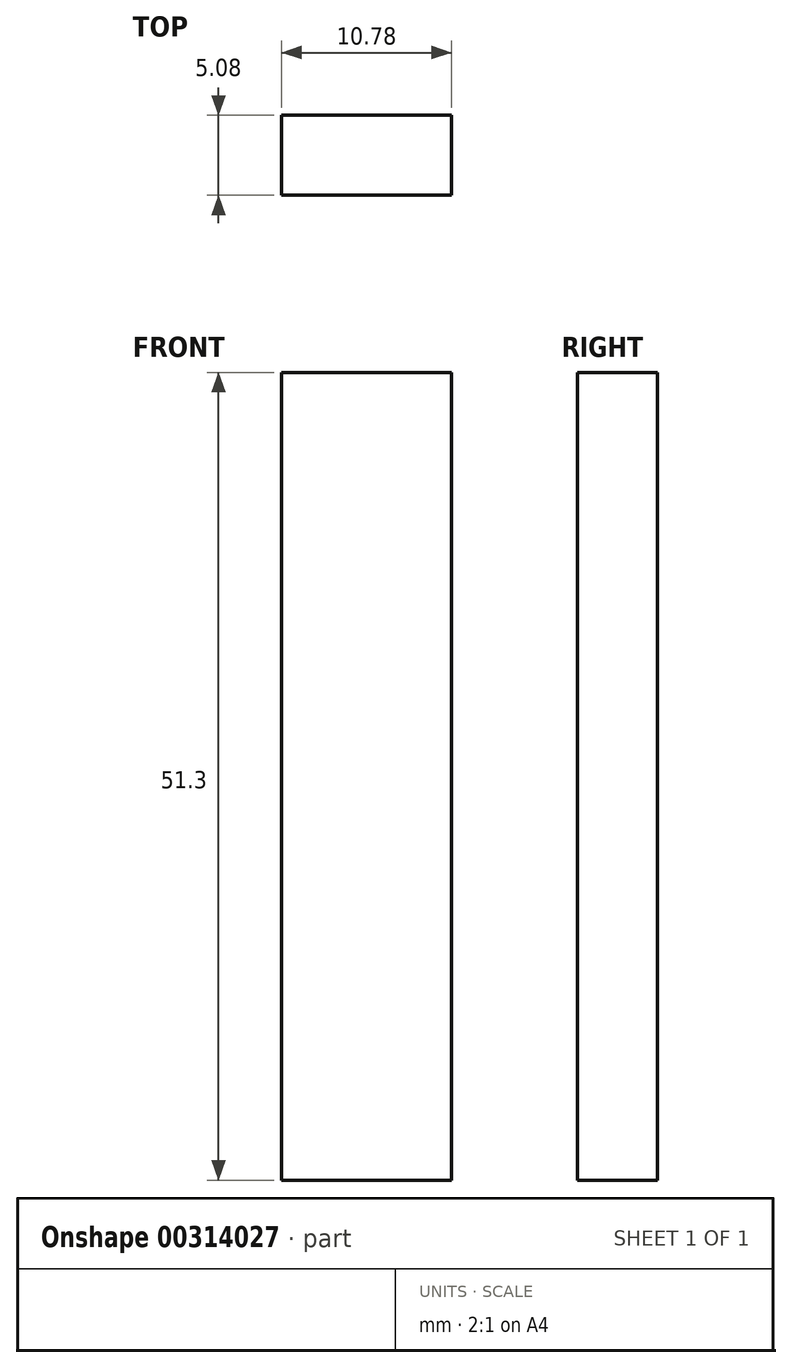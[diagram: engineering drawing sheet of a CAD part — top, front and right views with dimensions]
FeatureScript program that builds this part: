
annotation { "Feature Type Name" : "Feature", "Feature Type Description" : "" }
export const myFeature = defineFeature(function(context is Context, id is Id, definition is map)
    precondition{}
    {
        {
            var Q0;
            Q0=qCreatedBy(makeId("Front.planeOp"),FACE);
            var sketch = newSketch(context, id + "F0", { "sketchPlane" : qUnion([Q0])});
            skLineSegment(sketch, "E0.bottom", {"start": v(-27.1, 22.59) * mm, "end": v(-37.9, 22.59) * mm});
            skLineSegment(sketch, "E0.top", {"start": v(-27.1, -28.71) * mm, "end": v(-37.9, -28.71) * mm});
            skLineSegment(sketch, "E0.left", {"start": v(-27.1, 22.59) * mm, "end": v(-27.1, -28.71) * mm});
            skLineSegment(sketch, "E0.right", {"start": v(-37.9, 22.59) * mm, "end": v(-37.9, -28.71) * mm});
            skSolve(sketch);
        }
        {
            var Q0;
            Q0 = qSketchRegion(id + "F0", true);
            extrude(context, id + "F1", {"entities" : qUnion([Q0]), "depth" : 5.08 * mm});
        }
    });
